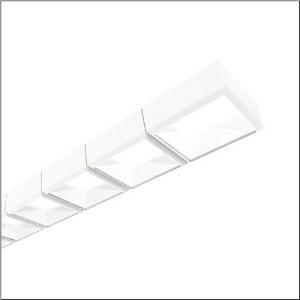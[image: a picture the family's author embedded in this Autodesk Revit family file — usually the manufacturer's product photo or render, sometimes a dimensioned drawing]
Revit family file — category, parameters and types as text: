
# Revit family: scriptus_r__11_5mz314d0twb_59a6
name_source: partatom
category: Lighting Fixtures
units: mm (PartAtom-declared; Revit-internal decimal feet)

## family parameters
Cut with Voids When Loaded = No
Host = Face
Light Source = No
Part Type = Normal
Room Calculation Point = No
Round Connector Dimension = Use Diameter
Shared = No

## types (1)
- --- (1 x LED 3000K+6500K / CRI = 80 (unbekannt), 3390 lm / 3600 lm, 3000K)
    Apparent Load = 106 VA
    CIE Flux Codes = 0 0 0 0 100 / 82 95 99 100 100
    Color Rendering = 80
    Color Temperature = 3000K
    Default Elevation = 1800 mm
    Description = Scriptus® 11, office luminaire, primary optical cover: lenses, CAT 2 (L<= 3000cd/m²), light emission: direct/indirect distribution, primary light characteristic: symmetric, installation type: suspended mounting, LED rated luminous flux: 13.970 lm, light colour: 8tw, colour temperature: 3000..6500K, control gear: ECG DALI, with terminal, 5-pole, mains connection: 230V, AC, 50Hz, rated input power: 110W, LED control gear: ECG DALI, housing, luminaire housing, of aluminium, traffic white (RAL 9016), length: 3.088 mm, width: 114 mm, height: 57mm, protection rating (complete): IP20, insulation class (complete): insulation class I (protective earthing), certification: CE, protection symbol: F, permissible ambient temperature for indoor applications: <= +25°C, standard: EN 50419, packaging unit: 1 piece
    Height = 57 mm
    Lamp = 1 x LED 3000K+6500K / CRI >= 80 (unbekannt)
    Lamp Light Flux = 3390 lm / 3600 lm
    Lamp count = 1
    Length = 3088 mm
    Luminous efficacy = 132 lm/W
    Manufacturer = Siteco
    ModVariant = No
    Model = 5MZ314D0TWB
    Mounting Place = Ceiling
    Mounting Type = Pendant
    Number of Poles = 1
    OnlyDefault = Yes
    Power Factor = 1
    Product Name = Scriptus® 11
    Product group = office luminaire | ceiling pendant
    ProductGroupID = 905
    Protection Class = Protection class I
    Protection Degree = IP 20
    RLX_Detail_Level = 1
    RlxData = <blob elided: 32365 chars, md5=a79f7d73>
    Socket = socket
    Standby Power = 0 W
    System Light Flux = 13980 lm
    System Power = 106 W
    Type Comments = individual setting: colour temperature 6500K
    Type Image = l_1004839.jpg
    URL = http://relux.com
    VarID = @adj_146248
    Voltage = 0 V
    Weight = 0.00 kg
    Width = 114 mm

## geometry (parser evidence)
native form markers: Blend x4, Sweep x20
no freeform markers — native parametric forms only
